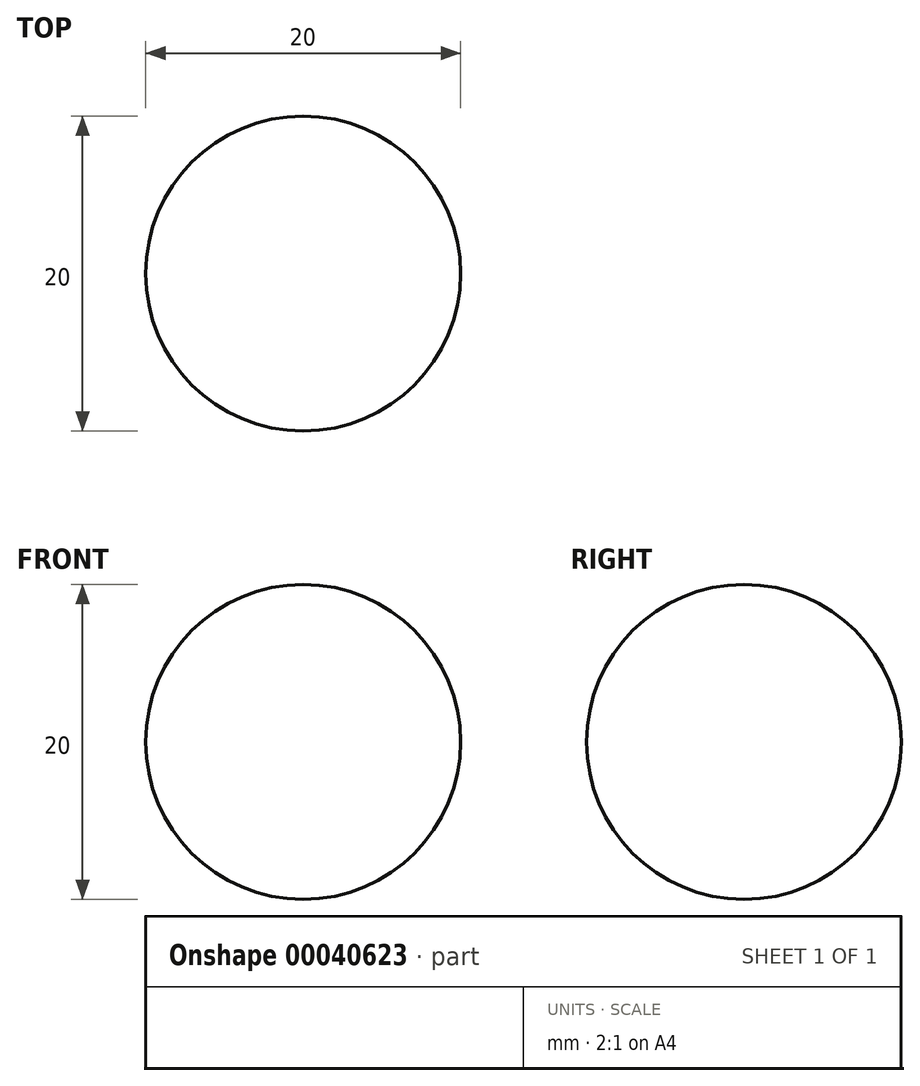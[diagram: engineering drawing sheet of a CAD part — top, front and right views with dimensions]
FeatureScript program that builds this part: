
annotation { "Feature Type Name" : "Feature", "Feature Type Description" : "" }
export const myFeature = defineFeature(function(context is Context, id is Id, definition is map)
    precondition{}
    {
        {
            var Q0;
            Q0=qCreatedBy(makeId("Top.planeOp"),FACE);
            var sketch = newSketch(context, id + "F0", { "sketchPlane" : qUnion([Q0])});
            skArc(sketch, "E0", {"start": v(10, 0) * mm, "mid": v(0, 10) * mm, "end": v(-10, 0) * mm});
            skLineSegment(sketch, "E1.top", {"start": v(-10, 0) * mm, "end": v(10, 0) * mm});
            skPoint(sketch, "E2.orphan", {"position": v(17.07, 0) * mm});
            skSolve(sketch);
        }
        {
            var Q0;
            Q0=qCreatedBy(makeId("Top.planeOp"),FACE);
            var sketch = newSketch(context, id + "F1", { "sketchPlane" : qUnion([Q0])});
            skLineSegment(sketch, "E3", {"start": v(0, 0) * mm, "end": v(19.7, 0) * mm});
            skSolve(sketch);
        }
        {
            var Q0;
            Q0=makeQuery(id+"F0.imprint","IMPRINT",FACE,{"disambiguationData":[TD([[makeQuery(id+"F0.imprint","IMPRINT",EDGE,{"derivedFrom":sQuery(id+"F0.wireOp",EDGE,"E0")}),1.0]])]});
            var Q1;
            Q1=sQuery(id+"F1.wireOp",EDGE,"E3");
            revolve(context, id + "F2", {"entities" : qUnion([Q0]), "axis" : qUnion([Q1]), "revolveType" : RevolveType.FULL});
        }
    });
